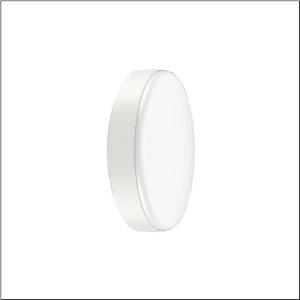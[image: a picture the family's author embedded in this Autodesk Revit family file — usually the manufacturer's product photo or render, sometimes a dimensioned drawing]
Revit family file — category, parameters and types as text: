
# Revit family: rondel_31_51wc10db44as
name_source: partatom
category: Lighting Fixtures
units: mm (PartAtom-declared; Revit-internal decimal feet)

## family parameters
Cut with Voids When Loaded = No
Host = Face
Light Source = No
Part Type = Normal
Room Calculation Point = No
Round Connector Dimension = Use Diameter
Shared = No

## types (1)
- Rondel 31 (1 x LED, 4400 lm, 35.5 W, 4000K)
    Apparent Load = 36 VA
    CIE Flux Codes = 44 75 94 94 100
    Color Rendering = 80
    Color Temperature = 4000K
    Default Elevation = 1800 mm
    Description = Rondel 31, wall and ceiling luminaire, primary optical cover: cover, of PC, opal, light emission: direct distribution, primary light characteristic: symmetric, installation type: surface-mounted, LED, rated luminous flux: 4.400lm, luminous efficacy: 124lm/W, light colour: 840, colour temperature: 4000K, with terminal, 3-pole, max. 2.5mm², mains connection: 220..240V, AC, 50/60Hz, rated input power: 35.5W, luminaire housing, of PC, traffic white (RAL 9016), diameter: 480mm, brightness and presence sensor, HF sensor, protection rating (complete): IP65, insulation class (complete): insulation class II (safety insulation), certification: CE, impact resistance: IK10, permissible operating ambient temperature: -20..+40°C, permissible storage temperature: -20..+60°C, packaging unit: 1 piece
    Height = 97 mm
    Lamp = 1 x LED
    Lamp Light Flux = 4400 lm
    Lamp Power = 35.5 W
    Lamp count = 1
    Length = 480 mm
    Luminous efficacy = 124 lm/W
    Manufacturer = Siteco
    ModVariant = No
    Model = 51WC10DB44AS
    Mounting Place = Ceiling
    Mounting Type = Surface mounted
    Number of Poles = 1
    OnlyDefault = Yes
    Power Factor = 1
    Product Name = Rondel 31
    Product group = wall and ceiling luminaire
    ProductGroupID = 301
    Protection Class = Protection class II
    Protection Degree = IP 65
    RLX_Detail_Level = 1
    RLX_Emergency_Light_Flux = 0 lm
    RLX_Emergency_Type = 0
    RLX_Emergency_Type_DB = No
    RlxData = <blob elided: 40821 chars, md5=2fdc028c>
    Socket = socket
    Standby Power = 0 W
    System Light Flux = 4400 lm
    System Power = 36 W
    Type Comments = Product without accessories
    Type Image = l_1007188.jpg
    URL = http://relux.com
    VarID = ---
    Voltage = 0 V
    Weight = 0.00 kg
    Width = 0 mm  [stored 0 ft]

note: [stored X ft] marks values corroborated as IEEE doubles in the binary element streams (Revit-internal decimal feet)

## geometry (parser evidence)
native form markers: Blend x4, Sweep x15
no freeform markers — native parametric forms only
